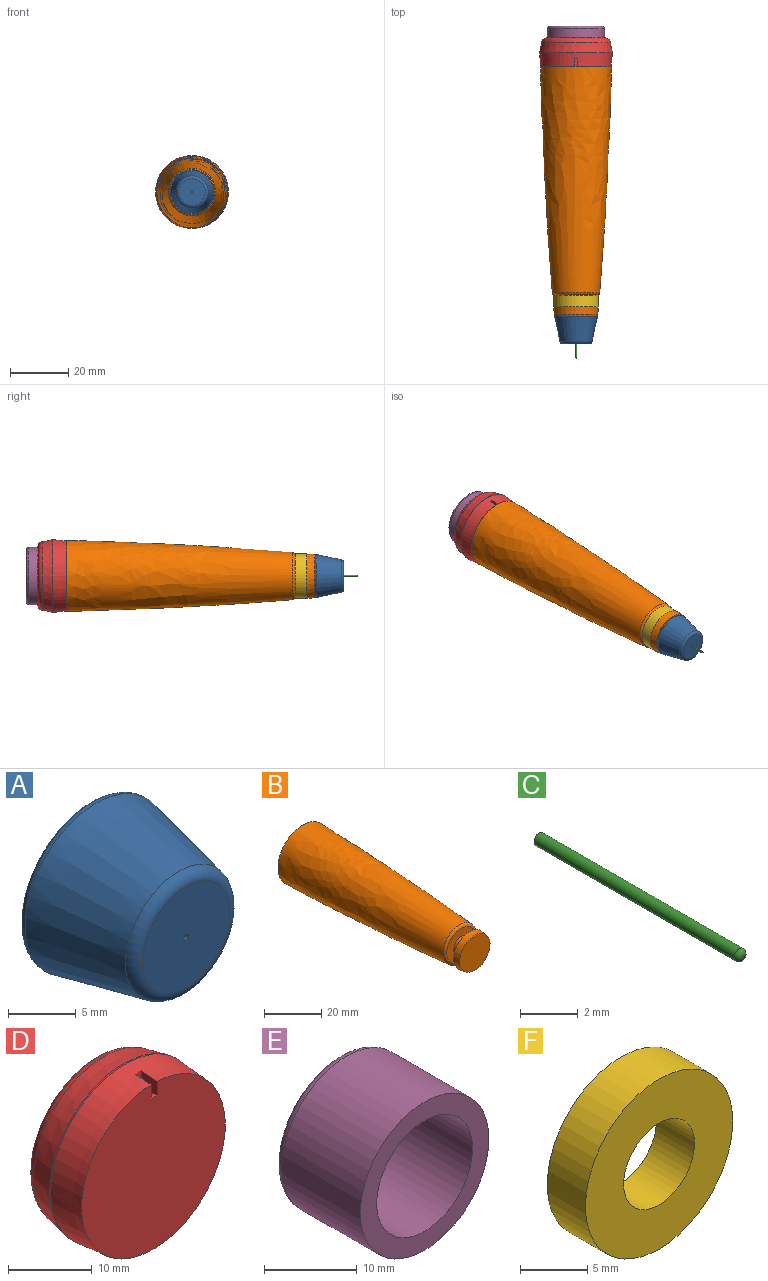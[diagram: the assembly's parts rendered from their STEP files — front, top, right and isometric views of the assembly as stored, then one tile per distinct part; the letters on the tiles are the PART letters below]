
ASSEMBLY  parts=6 mates=5
PART A: 11 faces, bbox 16x11.5x16 mm
  f0: torus R=4.55mm, axis (0,1,0), area 43.9mm2, adj f1,f4
  f1: plane 9.11x9.11mm, normal (0,-1,0), area 65mm2, adj f0,f5
  f2: plane 13.76x13.76mm, normal (0,1,0), area 72mm2, adj f3,f8
  f3: torus R=6.88mm, axis (0,1,0), area 40.4mm2, adj f2,f4
  f4: cone r=7.37mm half-angle=12.1deg, axis (0,1,0), area 356.7mm2, adj f0,f3
  f5: cylinder r=0.25mm len=9mm, axis (0,-1,0), area 14.1mm2, adj f1,f6
  f6: plane 0.5x0.5mm, normal (0,-1,0), area 0.2mm2, adj f5
  f7: plane 6.68x6.68mm, normal (0,1,0), area 11.3mm2, adj f8,f9
  f8: cone r=4.93mm half-angle=12.1deg, axis (0,1,0), area 199.6mm2, adj f2,f7
  f9: cylinder r=2.75mm len=9mm, axis (0,-1,0), area 155.5mm2, adj f7,f10
  f10: plane 5.5x5.5mm, normal (0,1,0), area 23.8mm2, adj f9
PART B: 12 faces, bbox 24.4x85x24.4 mm
  f0: plane 24.4x24.4mm, normal (0,1,0), area 172mm2, adj f1,f9
  f1: revolved ~77.39x24.4mm, area 5136.8mm2, adj f0,f2
  f2: torus R=7.15mm, axis (0,-1,0), area 72.7mm2, adj f1,f3
  f3: plane 14.31x14.31mm, normal (0,-1,0), area 116.9mm2, adj f2,f4
  f4: cylinder r=3.74mm len=7.47mm, axis (0,-1,0), area 93.9mm2, adj f3,f5
  f5: plane 15.47x15.47mm, normal (0,1,0), area 144.1mm2, adj f4,f6
  f6: cone r=7.5mm half-angle=5deg, axis (0,1,0), area 129.4mm2, adj f5,f7
  f7: plane 15x15mm, normal (0,-1,0), area 176.7mm2, adj f6
  f8: plane 2.47x2.47mm, normal (0,1,0), area 4.8mm2, adj f11
  f9: revolved ~75.81x19.4mm, area 3860.6mm2, adj f0,f10
  f10: plane 11.54x11.54mm, normal (0,1,0), area 99.8mm2, adj f9,f11
  f11: cylinder r=1.24mm len=6.69mm, axis (0,-1,0), area 51.9mm2, adj f8,f10
PART C: 4 faces, bbox 0.5x10x0.5 mm
  f0: cylinder r=0.25mm len=9.8mm, axis (0,1,0), area 15.4mm2, adj f2,f3
  f1: plane 0.1x0.1mm, normal (0,-1,0), area 0mm2, adj f3
  f2: plane 0.5x0.5mm, normal (0,1,0), area 0.2mm2, adj f0
  f3: torus R=0.05mm, axis (0,-1,0), area 0.4mm2, adj f0,f1
PART D: 11 faces, bbox 27.1x10x27.1 mm
  f0: revolved ~25x25mm, area 368.3mm2, adj f1,f4,f7,f8,f9
  f1: plane 24.2x24.19mm, normal (0,-1,0), area 457.7mm2, adj f0,f7,f8,f10
  f2: torus R=9.82mm, axis (0,1,0), area 188.6mm2, adj f3,f5
  f3: cone r=12.48mm half-angle=11.7deg, axis (0,-1,0), area 265.1mm2, adj f2,f4
  f4: torus R=11.5mm, axis (0,1,0), area 16mm2, adj f0,f3
  f5: cylinder r=9.82mm len=19.63mm, axis (0,1,0), area 555mm2, adj f2,f6
  f6: plane 19.63x19.63mm, normal (0,1,0), area 302.7mm2, adj f5
  f7: plane 2.68x2.27mm, normal (1,0,0), area 5.8mm2, adj f0,f1,f9,f10
  f8: plane 2.68x2.26mm, normal (-1,0,0), area 5.8mm2, adj f0,f1,f9,f10
  f9: plane 2.28x1mm, normal (0,-1,0), area 2.3mm2, adj f0,f7,f8,f10
  f10: plane 2.68x1mm, normal (0,0,1), area 2.7mm2, adj f1,f7,f8,f9
PART E: 6 faces, bbox 21.2x13x21.2 mm
  f0: cylinder r=9.82mm len=19.63mm, axis (0,1,0), area 740.1mm2, adj f1,f3
  f1: plane 19.63x19.63mm, normal (0,-1,0), area 134.5mm2, adj f0,f4
  f2: plane 17.63x17.63mm, normal (0,1,0), area 244.1mm2, adj f3
  f3: torus R=8.82mm, axis (0,-1,0), area 93.3mm2, adj f0,f2
  f4: cylinder r=7.32mm len=14.63mm, axis (0,1,0), area 482.6mm2, adj f1,f5
  f5: plane 14.63x14.63mm, normal (0,-1,0), area 168.1mm2, adj f4
PART F: 4 faces, bbox 15.4x4x15.4 mm
  f0: cylinder r=3.72mm len=7.43mm, axis (0,1,0), area 93.4mm2, adj f2,f3
  f1: cylinder r=7.72mm len=15.43mm, axis (0,1,0), area 193.9mm2, adj f2,f3
  f2: plane 15.43x15.43mm, normal (0,-1,0), area 143.7mm2, adj f0,f1
  f3: plane 15.43x15.43mm, normal (0,1,0), area 143.7mm2, adj f0,f1
PLACE A t=(-4.26,-85.69,13.94)mm
PLACE B t=(-4.26,-38.19,10.19)mm
PLACE C t=(-4.26,-85.59,10.19)mm
PLACE D t=(-10.51,9.31,10.19)mm
PLACE E t=(-4.26,18.31,10.19)mm
PLACE F t=(-4.26,-73.99,10.19)mm
MATE revolute D.f3 <-> B.f2  axis (0,-1,0) through (-4.26,4.31,10.19)mm
MATE fastened A.f0 <-> B.f2  axis (0,1,0) through (-4.26,-80.69,10.19)mm
MATE revolute E.f0 <-> D.f3  axis (0,-1,0) through (-4.26,5.31,10.19)mm
MATE fastened C.f0 <-> A.f0  axis (0,1,0) through (-4.26,-85.59,10.19)mm
MATE fastened F.f1 <-> B.f2  axis (0,1,0) through (-4.26,-73.99,10.19)mm
